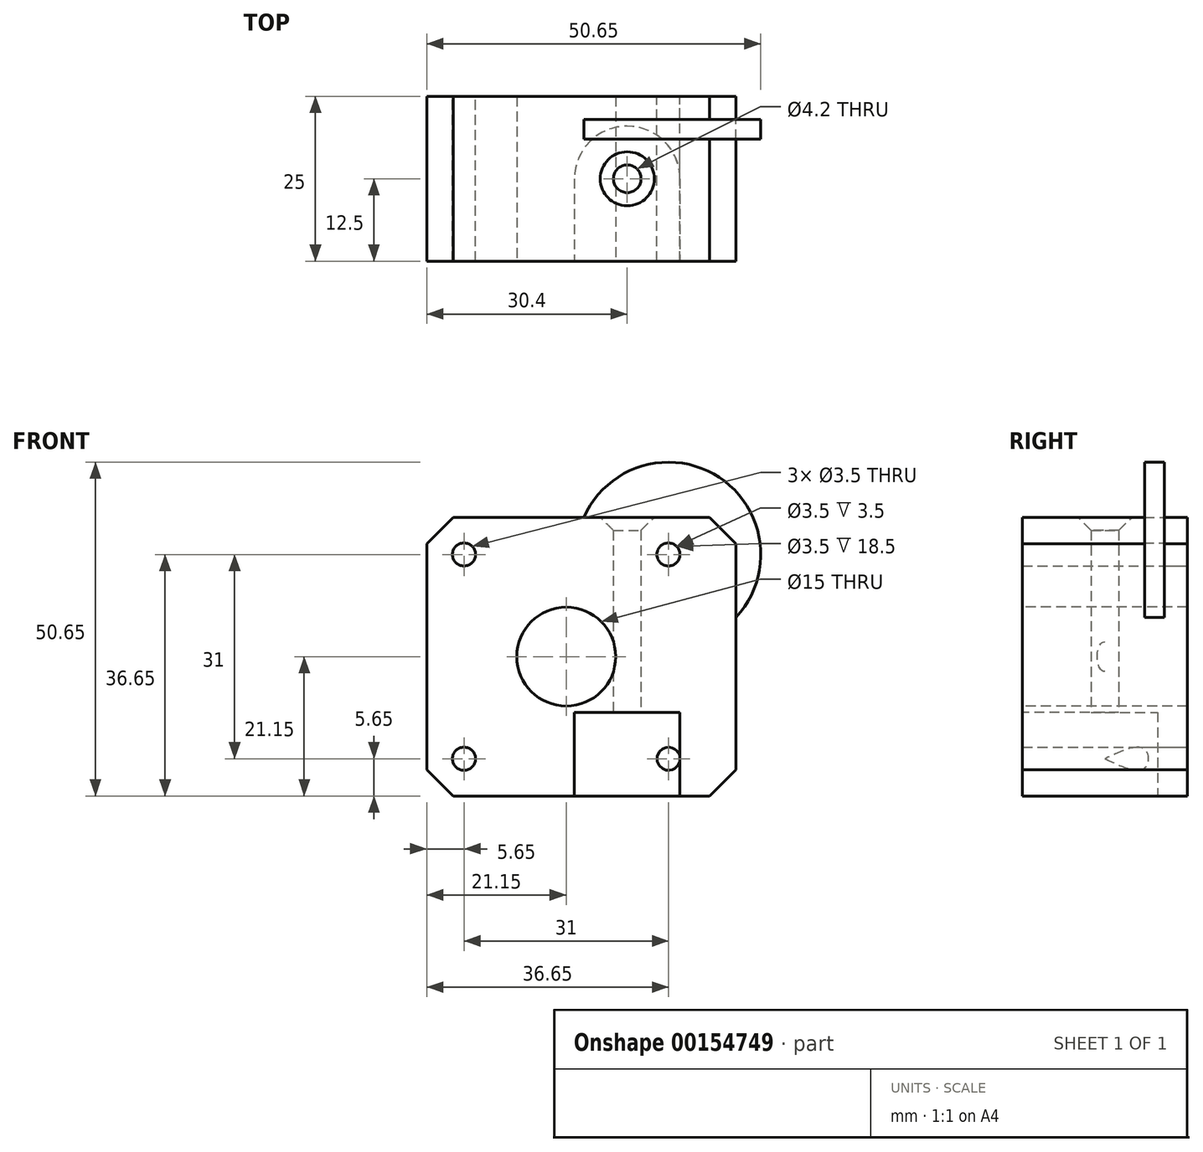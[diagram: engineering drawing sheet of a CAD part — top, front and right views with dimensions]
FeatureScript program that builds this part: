
annotation { "Feature Type Name" : "Feature", "Feature Type Description" : "" }
export const myFeature = defineFeature(function(context is Context, id is Id, definition is map)
    precondition{}
    {
        {
            var Q0;
            Q0=qCreatedBy(makeId("Front.planeOp"),FACE);
            var sketch = newSketch(context, id + "F0", { "sketchPlane" : qUnion([Q0])});
            skLineSegment(sketch, "E0.bottom", {"start": v(23.45, -21.15) * mm, "end": v(-23.45, -21.15) * mm});
            skLineSegment(sketch, "E0.top", {"start": v(23.45, 21.15) * mm, "end": v(-23.45, 21.15) * mm});
            skLineSegment(sketch, "E0.left", {"start": v(23.45, -21.15) * mm, "end": v(23.45, 21.15) * mm});
            skLineSegment(sketch, "E0.right", {"start": v(-23.45, -21.15) * mm, "end": v(-23.45, 21.15) * mm});
            skPoint(sketch, "E0.middle", {"position": v(0, 0) * mm});
            skCircle(sketch, "E1", {"center": v(-17.8, 15.5) * mm, "radius": 1.75 * mm});
            skCircle(sketch, "E2.0.1.0", {"center": v(-17.8, -15.5) * mm, "radius": 1.75 * mm});
            skCircle(sketch, "E2.1.0.0", {"center": v(13.2, 15.5) * mm, "radius": 1.75 * mm});
            skCircle(sketch, "E2.1.1.0", {"center": v(13.2, -15.5) * mm, "radius": 1.75 * mm});
            skLineSegment(sketch, "E2.direction1", {"start": v(-17.8, 15.5) * mm, "end": v(13.2, 15.5) * mm, "construction": true});
            skLineSegment(sketch, "E2.direction2", {"start": v(-17.8, 15.5) * mm, "end": v(-17.8, -15.5) * mm, "construction": true});
            skSolve(sketch);
        }
        {
            var Q0;
            Q0=makeQuery(id+"F0.imprint","IMPRINT",FACE,{"disambiguationData":[TD([[makeQuery(id+"F0.imprint","IMPRINT",EDGE,{"derivedFrom":sQuery(id+"F0.wireOp",EDGE,"E0.bottom")}),-1.0]])]});
            extrude(context, id + "F1", {"entities" : qUnion([Q0]), "depth" : 25 * mm});
        }
        {
            var Q0;
            Q0=makeQuery(id+"F1.opExtrude","SWEPT_EDGE",EDGE,{"disambiguationData":[OSD([sQuery(id+"F0.wireOp",EDGE,"E0.top"),sQuery(id+"F0.wireOp",EDGE,"E0.right")])]});
            var Q1;
            Q1=makeQuery(id+"F1.opExtrude","SWEPT_EDGE",EDGE,{"disambiguationData":[OSD([sQuery(id+"F0.wireOp",EDGE,"E0.top"),sQuery(id+"F0.wireOp",EDGE,"E0.left")])]});
            var Q2;
            Q2=makeQuery(id+"F1.opExtrude","SWEPT_EDGE",EDGE,{"disambiguationData":[OSD([sQuery(id+"F0.wireOp",EDGE,"E0.bottom"),sQuery(id+"F0.wireOp",EDGE,"E0.left")])]});
            var Q3;
            Q3=makeQuery(id+"F1.opExtrude","SWEPT_EDGE",EDGE,{"disambiguationData":[OSD([sQuery(id+"F0.wireOp",EDGE,"E0.bottom"),sQuery(id+"F0.wireOp",EDGE,"E0.right")])]});
            chamfer(context, id + "F2", {"entities" : qUnion([Q0, Q1, Q2, Q3]), "width" : 4 * mm, "tangentPropagation" : true});
        }
        {
            var Q0;
            Q0=makeQuery(id+"F1.opExtrude","SWEPT_FACE",FACE,{"disambiguationData":[OSD([sQuery(id+"F0.wireOp",EDGE,"E0.bottom")])]});
            var sketch = newSketch(context, id + "F3", { "sketchPlane" : qUnion([Q0])});
            skCircle(sketch, "E3", {"center": v(6.95, 12.5) * mm, "radius": 8 * mm});
            skLineSegment(sketch, "E4", {"start": v(6.95, 12.5) * mm, "end": v(-1.05, 12.5) * mm});
            skLineSegment(sketch, "E5", {"start": v(-1.05, 12.5) * mm, "end": v(-1.05, 25) * mm});
            skLineSegment(sketch, "E6", {"start": v(6.95, 12.5) * mm, "end": v(14.95, 12.5) * mm});
            skLineSegment(sketch, "E7", {"start": v(14.95, 12.5) * mm, "end": v(14.95, 25) * mm});
            skLineSegment(sketch, "E8", {"start": v(14.95, 25) * mm, "end": v(-1.05, 25) * mm});
            skSolve(sketch);
        }
        {
            var Q0;
            {var subQ0=sQuery(id+"F3.wireOp",EDGE,"E4");Q0=makeQuery(id+"F3.imprint","IMPRINT",FACE,{"disambiguationData":[TD([[makeQuery(id+"F3.imprint","IMPRINT",EDGE,{"derivedFrom":subQ0}),-1.0]])]});}
            var Q1;
            {var subQ0=sQuery(id+"F3.wireOp",EDGE,"E4");Q1=makeQuery(id+"F3.imprint","IMPRINT",FACE,{"disambiguationData":[TD([[makeQuery(id+"F3.imprint","IMPRINT",EDGE,{"derivedFrom":subQ0}),1.0]])]});}
            var Q2;
            {var subQ0=sQuery(id+"F3.wireOp",EDGE,"E5");Q2=makeQuery(id+"F3.imprint","IMPRINT",FACE,{"disambiguationData":[TD([[makeQuery(id+"F3.imprint","IMPRINT",EDGE,{"derivedFrom":subQ0}),-1.0]])]});}
            extrude(context, id + "F4", {"entities" : qUnion([Q0, Q1, Q2]), "operationType" : NewBodyOperationType.REMOVE, "oppositeDirection" : true, "depth" : 12.7 * mm});
        }
        {
            var Q0;
            Q0=makeQuery(id+"F4.boolean.opBoolean","COPY",FACE,{"derivedFrom":makeQuery(id+"F4.opExtrude","CAP_FACE",FACE,{"disambiguationData":[OSD([sQuery(id+"F3.wireOp",EDGE,"E3"),sQuery(id+"F3.wireOp",EDGE,"E5"),sQuery(id+"F3.wireOp",EDGE,"E7"),sQuery(id+"F3.wireOp",EDGE,"E8")])],"isStart":false})});
            var sketch = newSketch(context, id + "F5", { "sketchPlane" : qUnion([Q0])});
            skCircle(sketch, "E9", {"center": v(6.95, 12.5) * mm, "radius": 2.1 * mm});
            skSolve(sketch);
        }
        {
            var Q0;
            Q0 = qSketchRegion(id + "F5", true);
            extrude(context, id + "F6", {"entities" : qUnion([Q0]), "operationType" : NewBodyOperationType.REMOVE, "endBound" : BoundingType.THROUGH_ALL, "oppositeDirection" : true, "depth" : 25 * mm});
        }
        {
            var Q0;
            Q0=makeQuery(id+"F6.boolean.opBoolean","COPY",EDGE,{"derivedFrom":makeQuery(id+"F6.opExtrude","CAP_EDGE",EDGE,{"disambiguationData":[OSD([sQuery(id+"F5.wireOp",EDGE,"E9")])],"isStart":true})});
            var Q1;
            Q1=makeQuery(id+"F6.boolean.opBoolean","INTERSECT",EDGE,{"derivedFrom":[makeQuery(id+"F1.opExtrude","SWEPT_FACE",FACE,{"disambiguationData":[OSD([sQuery(id+"F0.wireOp",EDGE,"E0.top")])]}),makeQuery(id+"F6.opExtrude","SWEPT_FACE",FACE,{"disambiguationData":[OSD([sQuery(id+"F5.wireOp",EDGE,"E9")])]})]});
            chamfer(context, id + "F7", {"entities" : qUnion([Q0, Q1]), "width" : 2 * mm, "tangentPropagation" : true});
        }
        {
            var Q0;
            Q0=makeQuery(id+"F1.opExtrude","CAP_FACE",FACE,{"disambiguationData":[OSD([sQuery(id+"F0.wireOp",EDGE,"E0.bottom"),sQuery(id+"F0.wireOp",EDGE,"E0.top"),sQuery(id+"F0.wireOp",EDGE,"E0.left"),sQuery(id+"F0.wireOp",EDGE,"E0.right"),sQuery(id+"F0.wireOp",EDGE,"E1"),sQuery(id+"F0.wireOp",EDGE,"E2.0.1.0"),sQuery(id+"F0.wireOp",EDGE,"E2.1.0.0"),sQuery(id+"F0.wireOp",EDGE,"E2.1.1.0")])],"isStart":false});
            var sketch = newSketch(context, id + "F8", { "sketchPlane" : qUnion([Q0])});
            skLineSegment(sketch, "E10", {"start": v(-17.8, 15.5) * mm, "end": v(13.2, 15.5) * mm});
            skLineSegment(sketch, "E11", {"start": v(13.2, 15.5) * mm, "end": v(-17.8, -15.5) * mm});
            skLineSegment(sketch, "E12", {"start": v(-17.8, -15.5) * mm, "end": v(13.2, -15.5) * mm});
            skLineSegment(sketch, "E13", {"start": v(13.2, -15.5) * mm, "end": v(-17.8, 15.5) * mm});
            skCircle(sketch, "E14", {"center": v(-2.3, 0) * mm, "radius": 7.5 * mm});
            skSolve(sketch);
        }
        {
            var Q0;
            {var subQ0=sQuery(id+"F8.wireOp",EDGE,"E14");var subQ1=sQuery(id+"F3.wireOp",EDGE,"E8");var subQ4=makeQuery(id+"F4.boolean.opBoolean","COPY",EDGE,{"derivedFrom":makeQuery(id+"F4.opExtrude","CAP_EDGE",EDGE,{"disambiguationData":[OSD([subQ1])],"isStart":false})});var subQ5=makeQuery(id+"F8.imprint","INTERSECT",VERTEX,{"derivedFrom":[subQ4,subQ0]});Q0=makeQuery(id+"F8.imprint","IMPRINT",FACE,{"disambiguationData":[TD([[makeQuery(id+"F8.imprint","IMPRINT",EDGE,{"disambiguationData":[TD([[subQ5,1.0]])],"derivedFrom":subQ0}),1.0]])]});}
            var Q1;
            {var subQ0=sQuery(id+"F8.wireOp",EDGE,"E13");var subQ1=sQuery(id+"F8.wireOp",EDGE,"E10");var subQ2=makeQuery(id+"F8.imprint","INTERSECT",VERTEX,{"derivedFrom":[subQ1,subQ0]});Q1=makeQuery(id+"F8.imprint","IMPRINT",FACE,{"disambiguationData":[TD([[makeQuery(id+"F8.imprint","IMPRINT",EDGE,{"disambiguationData":[TD([[subQ2,-1.0]])],"derivedFrom":subQ1}),-1.0]])]});}
            var Q2;
            {var subQ0=sQuery(id+"F8.wireOp",EDGE,"E11");var subQ1=sQuery(id+"F8.wireOp",EDGE,"E10");var subQ2=makeQuery(id+"F8.imprint","INTERSECT",VERTEX,{"derivedFrom":[subQ1,subQ0]});Q2=makeQuery(id+"F8.imprint","IMPRINT",FACE,{"disambiguationData":[TD([[makeQuery(id+"F8.imprint","IMPRINT",EDGE,{"disambiguationData":[TD([[subQ2,1.0]])],"derivedFrom":subQ1}),-1.0]])]});}
            var Q3;
            {var subQ0=sQuery(id+"F8.wireOp",EDGE,"E12");var subQ1=sQuery(id+"F8.wireOp",EDGE,"E11");var subQ2=makeQuery(id+"F8.imprint","INTERSECT",VERTEX,{"derivedFrom":[subQ1,subQ0]});Q3=makeQuery(id+"F8.imprint","IMPRINT",FACE,{"disambiguationData":[TD([[makeQuery(id+"F8.imprint","IMPRINT",EDGE,{"disambiguationData":[TD([[subQ2,1.0]])],"derivedFrom":subQ1}),1.0]])]});}
            var Q4;
            {var subQ0=sQuery(id+"F8.wireOp",EDGE,"E14");var subQ1=sQuery(id+"F8.wireOp",EDGE,"E11");var subQ2=makeQuery(id+"F8.imprint","INTERSECT",VERTEX,{"disambiguationData":[OD(0.0)],"derivedFrom":[subQ1,subQ0]});Q4=makeQuery(id+"F8.imprint","IMPRINT",FACE,{"disambiguationData":[TD([[makeQuery(id+"F8.imprint","IMPRINT",EDGE,{"disambiguationData":[TD([[subQ2,-1.0]])],"derivedFrom":subQ1}),1.0]])]});}
            var Q5;
            {var subQ0=sQuery(id+"F8.wireOp",EDGE,"E14");var subQ1=sQuery(id+"F8.wireOp",EDGE,"E11");var subQ2=makeQuery(id+"F8.imprint","INTERSECT",VERTEX,{"disambiguationData":[OD(0.0)],"derivedFrom":[subQ1,subQ0]});Q5=makeQuery(id+"F8.imprint","IMPRINT",FACE,{"disambiguationData":[TD([[makeQuery(id+"F8.imprint","IMPRINT",EDGE,{"disambiguationData":[TD([[subQ2,-1.0]])],"derivedFrom":subQ1}),-1.0]])]});}
            var Q6;
            {var subQ0=sQuery(id+"F8.wireOp",EDGE,"E13");var subQ1=sQuery(id+"F8.wireOp",EDGE,"E11");var subQ2=makeQuery(id+"F8.imprint","INTERSECT",VERTEX,{"derivedFrom":[subQ1,subQ0]});Q6=makeQuery(id+"F8.imprint","IMPRINT",FACE,{"disambiguationData":[TD([[makeQuery(id+"F8.imprint","IMPRINT",EDGE,{"disambiguationData":[TD([[subQ2,-1.0]])],"derivedFrom":subQ1}),-1.0]])]});}
            var Q7;
            {var subQ0=sQuery(id+"F8.wireOp",EDGE,"E13");var subQ1=sQuery(id+"F8.wireOp",EDGE,"E11");var subQ2=makeQuery(id+"F8.imprint","INTERSECT",VERTEX,{"derivedFrom":[subQ1,subQ0]});Q7=makeQuery(id+"F8.imprint","IMPRINT",FACE,{"disambiguationData":[TD([[makeQuery(id+"F8.imprint","IMPRINT",EDGE,{"disambiguationData":[TD([[subQ2,-1.0]])],"derivedFrom":subQ1}),1.0]])]});}
            extrude(context, id + "F9", {"entities" : qUnion([Q0, Q1, Q2, Q3, Q4, Q5, Q6, Q7]), "operationType" : NewBodyOperationType.REMOVE, "endBound" : BoundingType.THROUGH_ALL, "oppositeDirection" : true, "depth" : 25 * mm});
        }
        {
            var Q0;
            Q0=makeQuery(id+"F1.opExtrude","CAP_FACE",FACE,{"disambiguationData":[OSD([sQuery(id+"F0.wireOp",EDGE,"E0.bottom"),sQuery(id+"F0.wireOp",EDGE,"E0.top"),sQuery(id+"F0.wireOp",EDGE,"E0.left"),sQuery(id+"F0.wireOp",EDGE,"E0.right"),sQuery(id+"F0.wireOp",EDGE,"E1"),sQuery(id+"F0.wireOp",EDGE,"E2.0.1.0"),sQuery(id+"F0.wireOp",EDGE,"E2.1.0.0"),sQuery(id+"F0.wireOp",EDGE,"E2.1.1.0")])],"isStart":false});
            cPlane(context, id + "F10", {"entities" : qUnion([Q0]), "cplaneType" : CPlaneType.OFFSET, "offset" : 20 * mm, "oppositeDirection" : true, "width" : 150 * mm, "height" : 150 * mm});
        }
        {
            var Q0;
            Q0=qCreatedBy(id+"F10.planeOp",FACE);
            var sketch = newSketch(context, id + "F11", { "sketchPlane" : qUnion([Q0])});
            skCircle(sketch, "E15", {"center": v(13.2, 15.5) * mm, "radius": 14 * mm});
            skLineSegment(sketch, "E16", {"start": v(-2.3, 17.6) * mm, "end": v(-2.3, 0) * mm});
            skSolve(sketch);
        }
        {
            var Q0;
            Q0 = qSketchRegion(id + "F11", true);
            extrude(context, id + "F12", {"entities" : qUnion([Q0]), "operationType" : NewBodyOperationType.ADD, "depth" : 3 * mm, "symmetric" : true});
        }
    });
